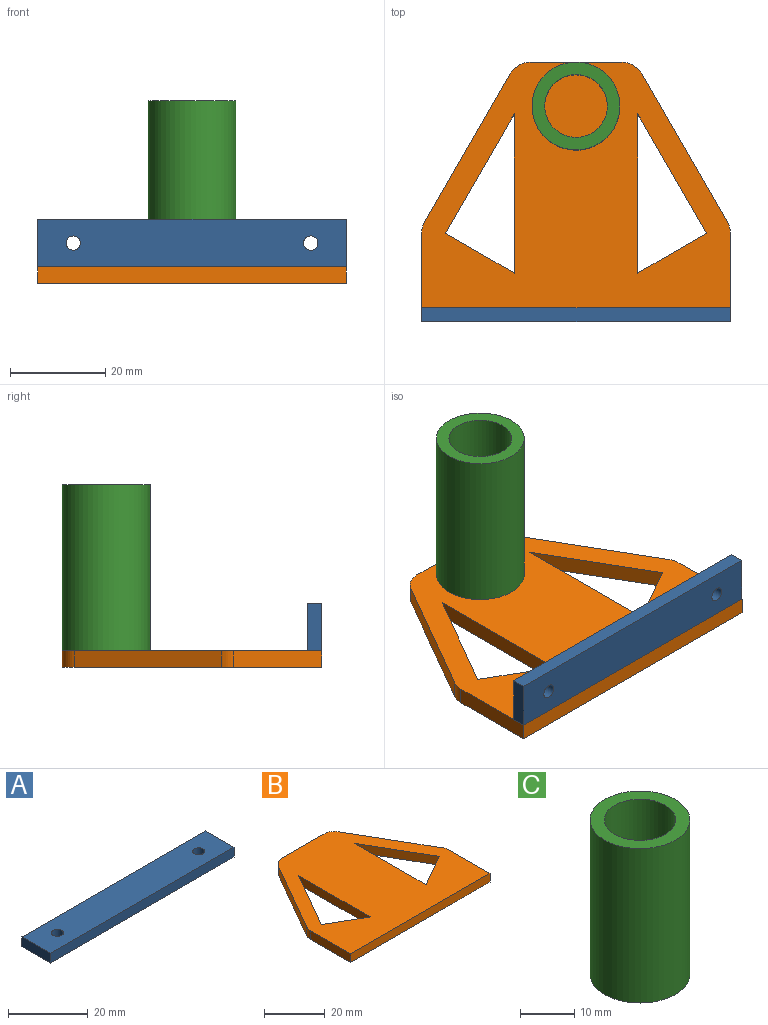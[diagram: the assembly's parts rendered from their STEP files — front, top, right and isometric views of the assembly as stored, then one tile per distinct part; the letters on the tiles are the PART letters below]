
ASSEMBLY  parts=3 mates=2
PART A: 8 faces, bbox 65x10x3 mm
  f0: plane 65x3mm, normal (0,1,0), area 195mm2, adj f1,f5,f6,f7
  f1: plane 10x3mm, normal (-1,0,0), area 30mm2, adj f0,f2,f6,f7
  f2: plane 65x3mm, normal (0,-1,0), area 195mm2, adj f1,f5,f6,f7
  f3: cylinder r=1.5mm len=3mm, axis (0,0,-1), area 28.3mm2, adj f6,f7
  f4: cylinder r=1.5mm len=3mm, axis (0,0,-1), area 28.3mm2, adj f6,f7
  f5: plane 10x3mm, normal (1,0,0), area 30mm2, adj f0,f2,f6,f7
  f6: plane 65x10mm, normal (0,0,1), area 635.9mm2, adj f0,f1,f2,f3,f4,f5
  f7: plane 65x10mm, normal (0,0,-1), area 635.9mm2, adj f0,f1,f2,f3,f4,f5
PART B: 18 faces, bbox 65x54.6x3.5 mm
  f0: cylinder r=5mm len=3.5mm, axis (0,0,-1), area 9.2mm2, adj f1,f15,f16,f17
  f1: plane 30.98x17.89mm, normal (0.87,0.5,0), area 125.2mm2, adj f0,f2,f16,f17
  f2: cylinder r=5mm len=4.33mm, axis (0,0,-1), area 18.3mm2, adj f1,f3,f16,f17
  f3: plane 19.23x3.5mm, normal (0,1,0), area 67.3mm2, adj f2,f4,f16,f17
  f4: cylinder r=5mm len=4.33mm, axis (0,0,-1), area 18.3mm2, adj f3,f5,f16,f17
  f5: plane 30.98x17.89mm, normal (-0.87,0.5,0), area 125.2mm2, adj f4,f6,f16,f17
  f6: cylinder r=5mm len=3.5mm, axis (0,0,-1), area 9.2mm2, adj f5,f7,f16,f17
  f7: plane 18.66x3.5mm, normal (-1,0,0), area 65.3mm2, adj f6,f8,f16,f17
  f8: plane 65x3.5mm, normal (0,-1,0), area 227.5mm2, adj f7,f15,f16,f17
  f9: plane 25.1x14.49mm, normal (-0.87,-0.5,0), area 101.5mm2, adj f10,f13,f16,f17
  f10: plane 14.49x8.37mm, normal (-0.5,0.87,0), area 58.6mm2, adj f9,f13,f16,f17
  f11: plane 14.49x8.37mm, normal (0.5,0.87,0), area 58.6mm2, adj f12,f14,f16,f17
  f12: plane 25.1x14.49mm, normal (0.87,-0.5,0), area 101.5mm2, adj f11,f14,f16,f17
  f13: plane 33.47x3.5mm, normal (1,0,0), area 117.2mm2, adj f9,f10,f16,f17
  f14: plane 33.47x3.5mm, normal (-1,0,0), area 117.2mm2, adj f11,f12,f16,f17
  f15: plane 18.66x3.5mm, normal (1,0,0), area 65.3mm2, adj f0,f8,f16,f17
  f16: plane 65x54.64mm, normal (0,0,1), area 2370.7mm2, adj f0,f1,f2,f3,f4,f5,f6,f7
  f17: plane 65x54.64mm, normal (0,0,-1), area 2370.7mm2, adj f0,f1,f2,f3,f4,f5,f6,f7
PART C: 4 faces, bbox 18.5x18.5x35 mm
  f0: cylinder r=6.6mm len=35mm, axis (0,0,-1), area 1451.4mm2, adj f2,f3
  f1: cylinder r=9.25mm len=35mm, axis (0,0,-1), area 2034.2mm2, adj f2,f3
  f2: plane 18.5x18.5mm, normal (0,0,1), area 132mm2, adj f0,f1
  f3: plane 18.5x18.5mm, normal (0,0,-1), area 132mm2, adj f0,f1
PLACE A rot(axis=(1,0,0),90deg) t=(-198.54,-117.84,165.48)mm
PLACE B t=(6.02,21.34,8.63)mm
PLACE C t=(-44.15,-127.34,12.13)mm
MATE fastened C.f0 <-> B.f16  axis (0,0,-1) through (-143.28,-75.45,12.13)mm
MATE fastened A.f2 <-> B.f16  axis (0,0,-1) through (-143.28,-119.34,12.13)mm
